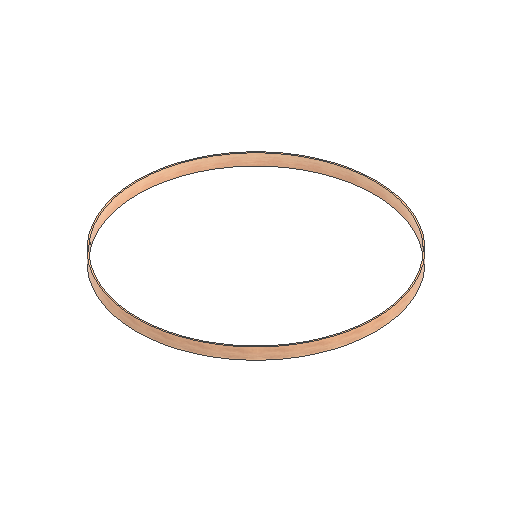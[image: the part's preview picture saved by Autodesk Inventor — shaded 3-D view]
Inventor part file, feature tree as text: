
AUTODESK INVENTOR PART (.ipt)
format: ipt  version: 2021 (Build 250183000, 183)  size: 108,032 bytes
history: native  units: mm
features: extrude x1, sketch x1
ambient origin geometry x8: Origin, YZ Plane, XZ Plane, XY Plane, X Axis, Y Axis, Z Axis, Center Point
bodies: Solid1 (feature_tree)
feature tree (2):
  extrude  "Extrusion1"  Depth=100.0mm
  sketch  "Sketch1"  dims[d0=2062.16mm d1=2084.16mm d2=100.0mm d3=0.0mm]
